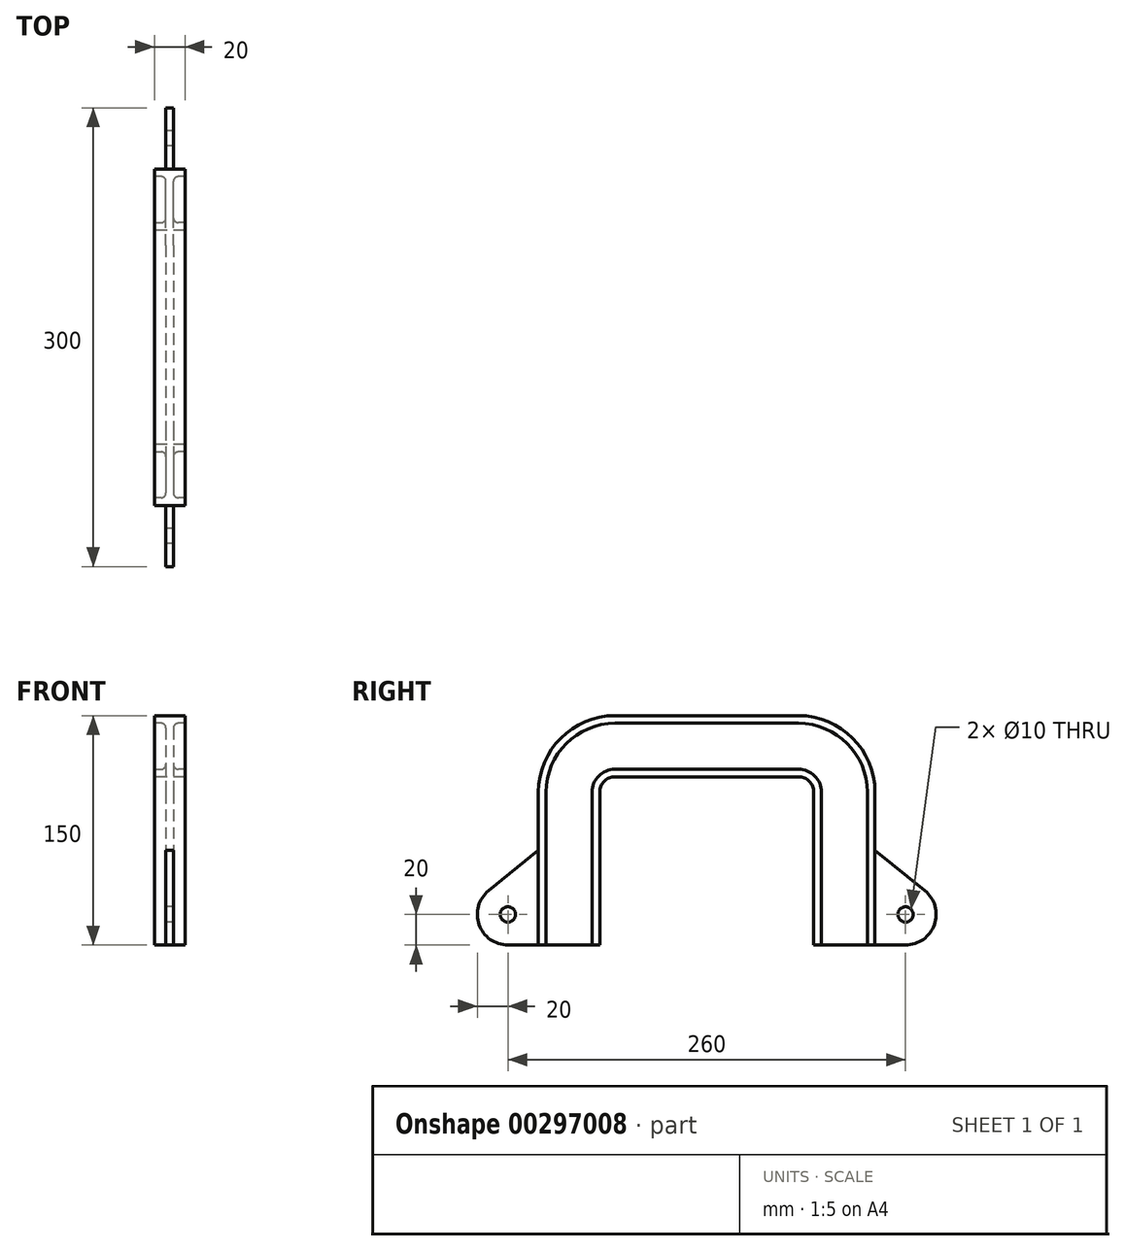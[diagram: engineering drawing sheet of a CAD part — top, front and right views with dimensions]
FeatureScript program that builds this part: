
annotation { "Feature Type Name" : "Feature", "Feature Type Description" : "" }
export const myFeature = defineFeature(function(context is Context, id is Id, definition is map)
    precondition{}
    {
        {
            var Q0;
            Q0=qCreatedBy(makeId("Front.planeOp"),FACE);
            var sketch = newSketch(context, id + "F0", { "sketchPlane" : qUnion([Q0])});
            skLineSegment(sketch, "E0", {"start": v(10, 0) * mm, "end": v(-10, 0) * mm});
            skLineSegment(sketch, "E1", {"start": v(-10, 0) * mm, "end": v(-10, 5) * mm});
            skLineSegment(sketch, "E2", {"start": v(10, 0) * mm, "end": v(10, 5) * mm});
            skLineSegment(sketch, "E3", {"start": v(-10, 5) * mm, "end": v(-5.5, 5) * mm});
            skLineSegment(sketch, "E4", {"start": v(10, 5) * mm, "end": v(5.5, 5) * mm});
            skArc(sketch, "E5", {"start": v(-5.5, 5) * mm, "mid": v(-3.38, 5.88) * mm, "end": v(-2.5, 8) * mm});
            skArc(sketch, "E6", {"start": v(5.5, 5) * mm, "mid": v(3.38, 5.88) * mm, "end": v(2.5, 8) * mm});
            skLineSegment(sketch, "E7", {"start": v(-2.5, 8) * mm, "end": v(-2.5, 32) * mm});
            skLineSegment(sketch, "E8", {"start": v(2.5, 8) * mm, "end": v(2.5, 32) * mm});
            skArc(sketch, "E9", {"start": v(-2.5, 32) * mm, "mid": v(-3.38, 34.12) * mm, "end": v(-5.5, 35) * mm});
            skArc(sketch, "E10", {"start": v(2.5, 32) * mm, "mid": v(3.38, 34.12) * mm, "end": v(5.5, 35) * mm});
            skLineSegment(sketch, "E11", {"start": v(-5.5, 35) * mm, "end": v(-10, 35) * mm});
            skLineSegment(sketch, "E12", {"start": v(-10, 35) * mm, "end": v(-10, 40) * mm});
            skLineSegment(sketch, "E13", {"start": v(-10, 40) * mm, "end": v(10, 40) * mm});
            skLineSegment(sketch, "E14", {"start": v(10, 40) * mm, "end": v(10, 35) * mm});
            skLineSegment(sketch, "E15", {"start": v(10, 35) * mm, "end": v(5.5, 35) * mm});
            skSolve(sketch);
        }
        {
            var Q0;
            Q0=qCreatedBy(makeId("Right.planeOp"),FACE);
            var sketch = newSketch(context, id + "F1", { "sketchPlane" : qUnion([Q0])});
            skLineSegment(sketch, "E16", {"start": v(-70, -110) * mm, "end": v(-70, -10) * mm});
            skArc(sketch, "E17", {"start": v(-70, -10) * mm, "mid": v(-67.07, -2.93) * mm, "end": v(-60, 0) * mm});
            skLineSegment(sketch, "E18", {"start": v(-60, 0) * mm, "end": v(0, 0) * mm});
            skSolve(sketch);
        }
        {
            var Q0;
            Q0=qCreatedBy(makeId("Right.planeOp"),FACE);
            var sketch = newSketch(context, id + "F2", { "sketchPlane" : qUnion([Q0])});
            skLineSegment(sketch, "E19", {"start": v(-100, -110) * mm, "end": v(-130, -110) * mm});
            skArc(sketch, "E20", {"start": v(-130, -110) * mm, "mid": v(-148.85, -96.67) * mm, "end": v(-142.58, -74.45) * mm});
            skLineSegment(sketch, "E21", {"start": v(-142.58, -74.45) * mm, "end": v(-100, -40) * mm});
            skLineSegment(sketch, "E22", {"start": v(-100, -40) * mm, "end": v(-100, -110) * mm});
            skCircle(sketch, "E23", {"center": v(-130, -90) * mm, "radius": 5 * mm});
            skSolve(sketch);
        }
        {
            var Q0;
            Q0 = qSketchRegion(id + "F0", true);
            var Q1;
            Q1 = qConstructionFilter(qBodyType(qCreatedBy(id + "F1" ,EDGE), BodyType.WIRE), ConstructionObject.NO);
            sweep(context, id + "F3", {"profiles" : qUnion([Q0]), "path" : qUnion([Q1])});
        }
        {
            var Q0;
            Q0=makeQuery(id+"F3.opSweep","SWEPT_BODY",BODY,{"disambiguationData":[OSD([sQuery(id+"F0.wireOp",EDGE,"E0"),sQuery(id+"F0.wireOp",EDGE,"E1"),sQuery(id+"F0.wireOp",EDGE,"E2"),sQuery(id+"F0.wireOp",EDGE,"E3"),sQuery(id+"F0.wireOp",EDGE,"E4"),sQuery(id+"F0.wireOp",EDGE,"E5"),sQuery(id+"F0.wireOp",EDGE,"E6"),sQuery(id+"F0.wireOp",EDGE,"E7"),sQuery(id+"F0.wireOp",EDGE,"E8"),sQuery(id+"F0.wireOp",EDGE,"E9"),sQuery(id+"F0.wireOp",EDGE,"E10"),sQuery(id+"F0.wireOp",EDGE,"E11"),sQuery(id+"F0.wireOp",EDGE,"E12"),sQuery(id+"F0.wireOp",EDGE,"E13"),sQuery(id+"F0.wireOp",EDGE,"E14"),sQuery(id+"F0.wireOp",EDGE,"E15"),sQuery(id+"F1.wireOp",EDGE,"E18")])]});
            var Q1;
            Q1=qCreatedBy(makeId("Front.planeOp"),FACE);
            mirror(context, id + "F4", {"operationType" : NewBodyOperationType.ADD, "entities" : qUnion([Q0]), "mirrorPlane" : qUnion([Q1])});
        }
        {
            var Q0;
            Q0=makeQuery(id+"F2.imprint","IMPRINT",FACE,{"disambiguationData":[TD([[makeQuery(id+"F2.imprint","IMPRINT",EDGE,{"derivedFrom":sQuery(id+"F2.wireOp",EDGE,"E19")}),-1.0]])]});
            extrude(context, id + "F5", {"entities" : qUnion([Q0]), "operationType" : NewBodyOperationType.ADD, "endBound" : BoundingType.SYMMETRIC, "depth" : 5 * mm});
        }
        {
            var Q0;
            Q0=makeQuery(id+"F3.opSweep","SWEPT_BODY",BODY,{"disambiguationData":[OSD([sQuery(id+"F0.wireOp",EDGE,"E0"),sQuery(id+"F0.wireOp",EDGE,"E1"),sQuery(id+"F0.wireOp",EDGE,"E2"),sQuery(id+"F0.wireOp",EDGE,"E3"),sQuery(id+"F0.wireOp",EDGE,"E4"),sQuery(id+"F0.wireOp",EDGE,"E5"),sQuery(id+"F0.wireOp",EDGE,"E6"),sQuery(id+"F0.wireOp",EDGE,"E7"),sQuery(id+"F0.wireOp",EDGE,"E8"),sQuery(id+"F0.wireOp",EDGE,"E9"),sQuery(id+"F0.wireOp",EDGE,"E10"),sQuery(id+"F0.wireOp",EDGE,"E11"),sQuery(id+"F0.wireOp",EDGE,"E12"),sQuery(id+"F0.wireOp",EDGE,"E13"),sQuery(id+"F0.wireOp",EDGE,"E14"),sQuery(id+"F0.wireOp",EDGE,"E15"),sQuery(id+"F1.wireOp",EDGE,"E18")])]});
            var Q1;
            Q1=qCreatedBy(makeId("Front.planeOp"),FACE);
            mirror(context, id + "F6", {"operationType" : NewBodyOperationType.ADD, "entities" : qUnion([Q0]), "mirrorPlane" : qUnion([Q1])});
        }
    });
